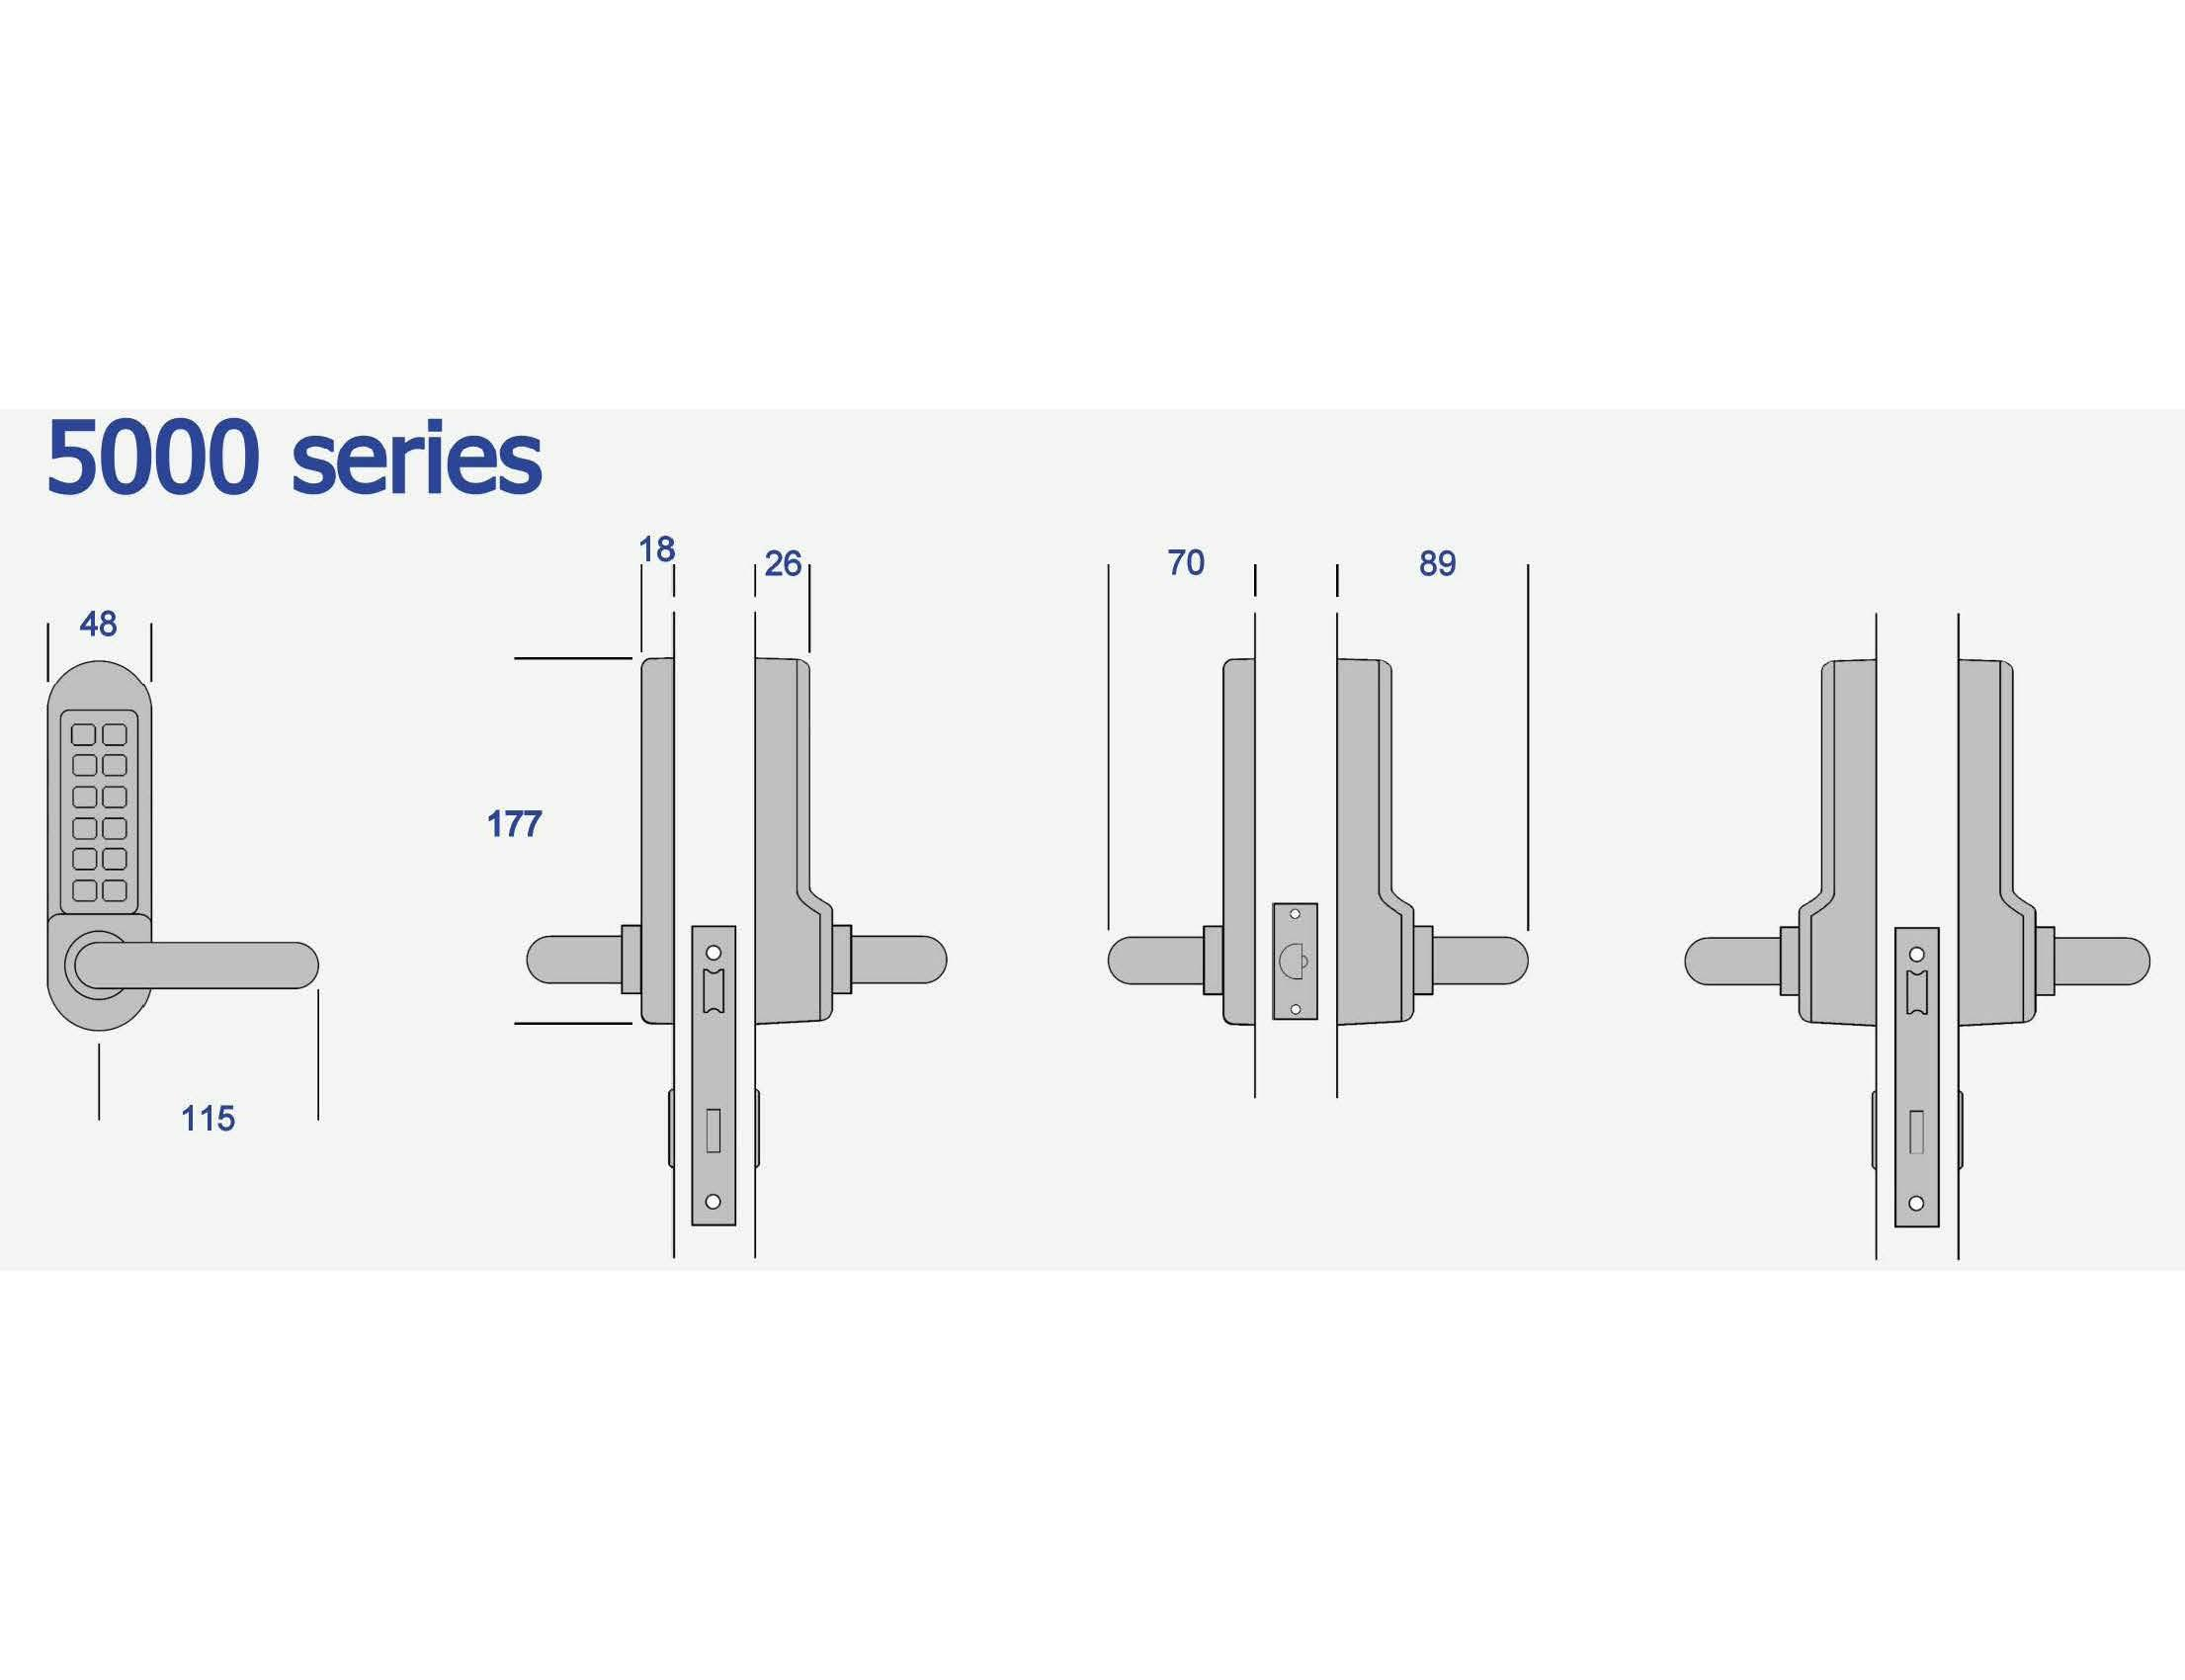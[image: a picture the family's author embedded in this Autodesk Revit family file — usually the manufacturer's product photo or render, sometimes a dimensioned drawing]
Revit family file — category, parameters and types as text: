
# Revit family: NBS_Lomax_Door_FDIN11-S
name_source: partatom
category: Doors
revit_build: Autodesk Revit Architecture 2016 (Build: 20150220_1215(x64)
units: mm (PartAtom-declared; Revit-internal decimal feet)

## family parameters
Always vertical = Yes
Cut with Voids When Loaded = No
Host = Wall
OmniClass Number = 23.30.10.00
OmniClass Title = Doors
Room Calculation Point = No
Shared = No

## types (1)
- NBS_Lomax_Door_FDIN11-S
    BIMObjectName = NBS_Lomax_Door_FDIN11-S
    Category = Doors
    Description = French Doors
    Frame Projection Ext. = 25 mm  [stored 0.082021 ft]
    Frame Projection Int. = 25 mm  [stored 0.082021 ft]
    Frame Width = 76 mm
    Function = Interior
    Glass = Glass
    Height = 2240 mm  [stored 7.34908 ft]
    Higes = Yes
    Hinges = Yes
    Lever Height from FFL = 1000 mm  [stored 3.28084 ft]
    Manufacturer = Lomax
    ManufacturerName = Lomax
    ManufacturerURL = lomaxwood.co.uk
    Model = NBS_Lomax_Door_FDIN11-S
    ModelNumber = FDIN11-S
    ModelReference = NBS_Lomax_Door_FDIN11-S
    NBSDescription = French Doors
    NBSNote = FDIN11-S
    NBSReference = NBS_Lomax_Door_FDIN11-S
    Name = FDIN11-S
    NominalHeight = 2240 mm  [stored 7.34908 ft]
    NominalLength = 76 mm
    NominalWidth = 1480 mm  [stored 4.85564 ft]
    ProductInformation = French Doors
    Revision = 1
    Rough Height = 2240 mm  [stored 7.34908 ft]
    Rough Width = 620 mm
    Thickness = 76 mm
    URL = lomaxwood.co.uk
    Wall Closure = By host
    White = White
    White Wood = WHite Wood
    Width = 1480 mm  [stored 4.85564 ft]
    Wood Wood = Wood Wood

note: [stored X ft] marks values corroborated as IEEE doubles in the binary element streams (Revit-internal decimal feet)

## geometry (parser evidence)
native form markers: Blend x2, Sweep x18
no freeform markers — native parametric forms only
